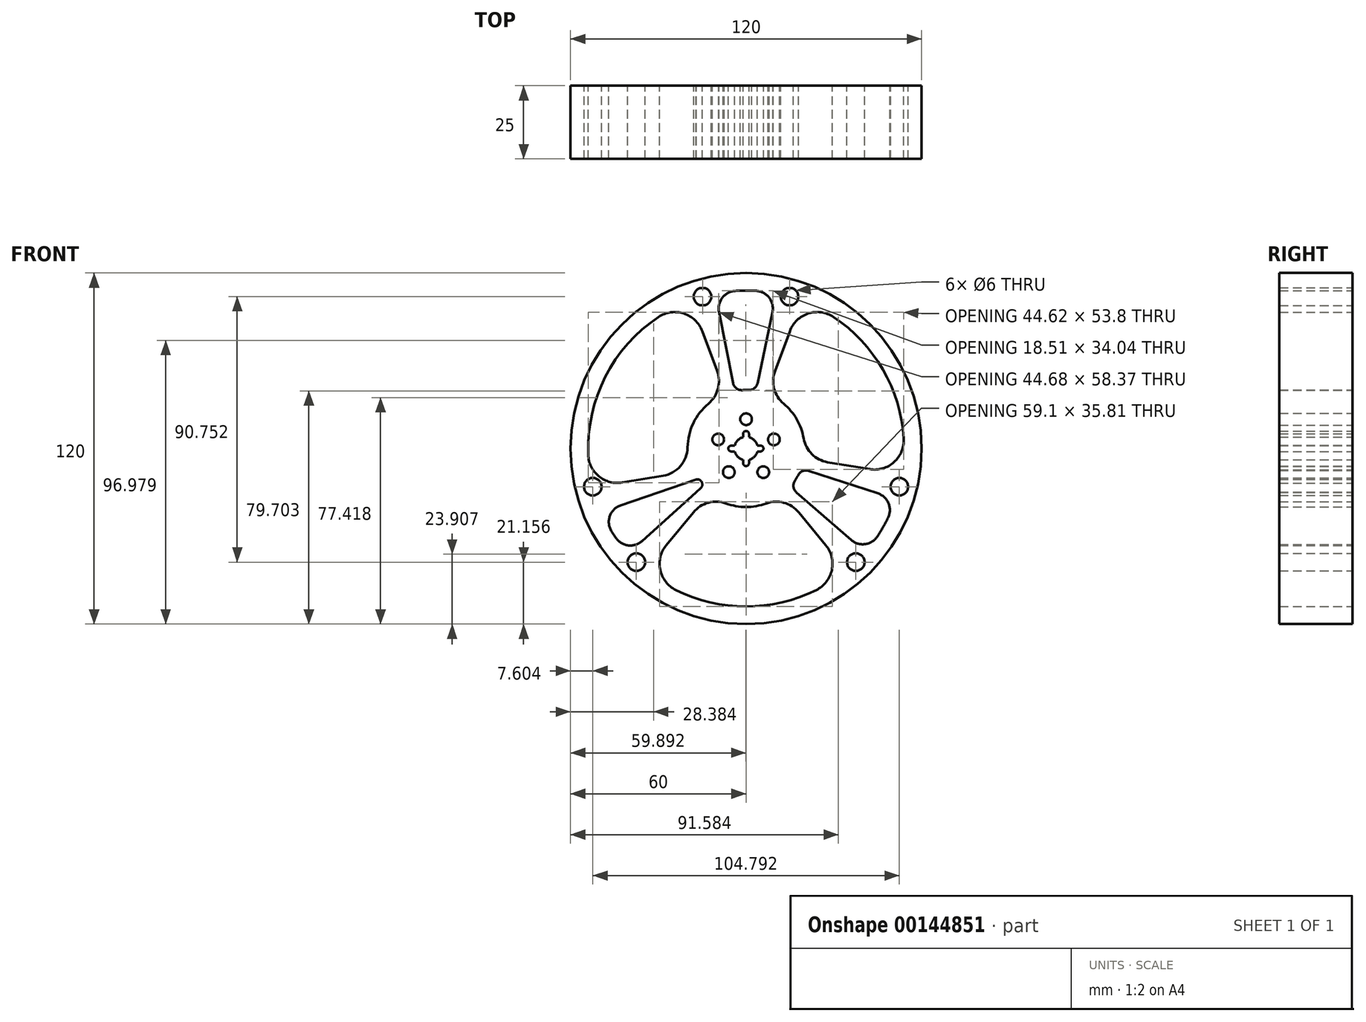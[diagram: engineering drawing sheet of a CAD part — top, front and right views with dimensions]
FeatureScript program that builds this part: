
annotation { "Feature Type Name" : "Feature", "Feature Type Description" : "" }
export const myFeature = defineFeature(function(context is Context, id is Id, definition is map)
    precondition{}
    {
        {
            var Q0;
            Q0=qCreatedBy(makeId("Front.planeOp"),FACE);
            var sketch = newSketch(context, id + "F0", { "sketchPlane" : qUnion([Q0])});
            skArc(sketch, "E0", {"start": v(-6, 0.32) * mm, "mid": v(-6, 0) * mm, "end": v(-6, -0.32) * mm, "construction": true});
            skArc(sketch, "E1", {"start": v(-1, 3.87) * mm, "mid": v(-2.83, 2.83) * mm, "end": v(-3.87, 1) * mm});
            skCircle(sketch, "E2", {"center": v(0, 0) * mm, "radius": 15 * mm});
            skArc(sketch, "E3", {"start": v(1, 5) * mm, "mid": v(0, 6) * mm, "end": v(-1, 5) * mm});
            skArc(sketch, "E4", {"start": v(4.95, -1) * mm, "mid": v(5.95, 0) * mm, "end": v(4.95, 1) * mm});
            skArc(sketch, "E5", {"start": v(-1, -5.01) * mm, "mid": v(0, -6.01) * mm, "end": v(1, -5.01) * mm});
            skArc(sketch, "E6", {"start": v(-5.05, 1) * mm, "mid": v(-6.05, 0) * mm, "end": v(-5.05, -1) * mm});
            skLineSegment(sketch, "E7", {"start": v(-1, 5) * mm, "end": v(-1, 3.87) * mm});
            skLineSegment(sketch, "E8", {"start": v(1, 5) * mm, "end": v(1, 3.87) * mm});
            skLineSegment(sketch, "E9", {"start": v(4.95, 1) * mm, "end": v(3.87, 1) * mm});
            skLineSegment(sketch, "E10", {"start": v(4.95, -1) * mm, "end": v(3.87, -1) * mm});
            skLineSegment(sketch, "E11", {"start": v(1, -5.01) * mm, "end": v(1, -3.87) * mm});
            skLineSegment(sketch, "E12", {"start": v(-1, -5.01) * mm, "end": v(-1, -3.87) * mm});
            skLineSegment(sketch, "E13", {"start": v(-5.05, 1) * mm, "end": v(-3.87, 1) * mm});
            skLineSegment(sketch, "E14", {"start": v(-5.05, -1) * mm, "end": v(-3.87, -1) * mm});
            skArc(sketch, "E15.trimOffspring", {"start": v(3.87, 1) * mm, "mid": v(2.83, 2.83) * mm, "end": v(1, 3.87) * mm});
            skArc(sketch, "E16.trimOffspring", {"start": v(1, -3.87) * mm, "mid": v(2.83, -2.83) * mm, "end": v(3.87, -1) * mm});
            skArc(sketch, "E17.trimOffspring", {"start": v(-3.87, -1) * mm, "mid": v(-2.83, -2.83) * mm, "end": v(-1, -3.87) * mm});
            skCircle(sketch, "E18", {"center": v(0, 10) * mm, "radius": 2 * mm});
            skPoint(sketch, "E18.centerSnap0", {"position": v(0, 6) * mm});
            skCircle(sketch, "E19.1.0", {"center": v(-9.51, 3.1) * mm, "radius": 2 * mm});
            skCircle(sketch, "E19.2.0", {"center": v(-5.88, -8.1) * mm, "radius": 2 * mm});
            skCircle(sketch, "E19.3.0", {"center": v(5.88, -8.1) * mm, "radius": 2 * mm});
            skCircle(sketch, "E19.4.0", {"center": v(9.51, 3.1) * mm, "radius": 2 * mm});
            skArc(sketch, "E20.trimOffspring", {"start": v(-0.17, -6) * mm, "mid": v(0, -6) * mm, "end": v(0.17, -6) * mm, "construction": true});
            skArc(sketch, "E21", {"start": v(-6.86, -18.79) * mm, "mid": v(0, -20) * mm, "end": v(6.86, -18.79) * mm});
            skArc(sketch, "E22", {"start": v(-46.03, -28.24) * mm, "mid": v(-45.3, -29.4) * mm, "end": v(-44.53, -30.55) * mm});
            skCircle(sketch, "E23", {"center": v(0, 0) * mm, "radius": 60 * mm});
            skLineSegment(sketch, "E24", {"start": v(-14.06, 49.02) * mm, "end": v(-14.88, 51.9) * mm, "construction": true});
            skCircle(sketch, "E25", {"center": v(14.88, 51.9) * mm, "radius": 3 * mm});
            skCircle(sketch, "E26", {"center": v(-14.88, 51.9) * mm, "radius": 3 * mm});
            skLineSegment(sketch, "E27", {"start": v(-9.9, 26.5) * mm, "end": v(-15, 40.14) * mm});
            skLineSegment(sketch, "E28", {"start": v(9.9, 26.5) * mm, "end": v(15, 40.14) * mm});
            skLineSegment(sketch, "E29", {"start": v(-9.25, 46.72) * mm, "end": v(-4.43, 22.37) * mm});
            skCircle(sketch, "E30.1.0", {"center": v(-37.51, -38.84) * mm, "radius": 3 * mm});
            skCircle(sketch, "E30.1.1", {"center": v(-52.4, -13.06) * mm, "radius": 3 * mm});
            skLineSegment(sketch, "E30.1.3", {"start": v(-35.57, -31.62) * mm, "end": v(-17.1, -15.02) * mm});
            skCircle(sketch, "E30.2.0", {"center": v(52.4, -13.06) * mm, "radius": 3 * mm});
            skCircle(sketch, "E30.2.1", {"center": v(37.51, -38.84) * mm, "radius": 3 * mm});
            skLineSegment(sketch, "E30.2.2", {"start": v(27.9, -4.68) * mm, "end": v(42.26, -7.08) * mm});
            skLineSegment(sketch, "E30.2.3", {"start": v(45, -15.32) * mm, "end": v(21.4, -7.64) * mm});
            skLineSegment(sketch, "E31.trimOffspring", {"start": v(-18, -21.82) * mm, "end": v(-27.27, -33.05) * mm});
            skLineSegment(sketch, "E32.trimOffspring", {"start": v(-17, -10.54) * mm, "end": v(-42.86, -19.43) * mm});
            skLineSegment(sketch, "E33.trimOffspring", {"start": v(-28.35, -9.3) * mm, "end": v(-42.32, -11.64) * mm});
            skLineSegment(sketch, "E34.trimOffspring", {"start": v(17.2, -14.97) * mm, "end": v(35.92, -31.27) * mm});
            skLineSegment(sketch, "E35.trimOffspring", {"start": v(18.01, -21.82) * mm, "end": v(27.27, -33.06) * mm});
            skPoint(sketch, "E36.orphan", {"position": v(-0.28, -0.58) * mm});
            skPoint(sketch, "E37.orphan", {"position": v(0, -0.02) * mm});
            skLineSegment(sketch, "E38.trimOffspring", {"start": v(3.94, 22.36) * mm, "end": v(9.02, 46.67) * mm});
            skArc(sketch, "E39.trimOffspring", {"start": v(3.54, 53.88) * mm, "mid": v(-0.12, 54) * mm, "end": v(-3.78, 53.87) * mm});
            skLineSegment(sketch, "E40.trimOffspring", {"start": v(14.06, 49.02) * mm, "end": v(14.88, 51.9) * mm, "construction": true});
            skArc(sketch, "E41.trimOffspring", {"start": v(-29.9, 44.97) * mm, "mid": v(-48.1, 24.54) * mm, "end": v(-53.96, -2.18) * mm});
            skArc(sketch, "E42.trimOffspring", {"start": v(-12.84, 15.33) * mm, "mid": v(-18.04, 8.63) * mm, "end": v(-20, 0.37) * mm});
            skArc(sketch, "E43.trimOffspring", {"start": v(0.87, 19.98) * mm, "mid": v(-0.21, 20) * mm, "end": v(-1.3, 19.96) * mm});
            skArc(sketch, "E44.trimOffspring", {"start": v(19.7, 3.46) * mm, "mid": v(17.32, 10) * mm, "end": v(12.84, 15.33) * mm});
            skArc(sketch, "E45.trimOffspring", {"start": v(16.67, -11.05) * mm, "mid": v(17.26, -10.1) * mm, "end": v(17.8, -9.12) * mm});
            skArc(sketch, "E46.trimOffspring", {"start": v(53.9, 3.42) * mm, "mid": v(46.76, 27) * mm, "end": v(29.9, 44.97) * mm});
            skArc(sketch, "E47.trimOffspring", {"start": v(44.84, -30.09) * mm, "mid": v(46.8, -26.94) * mm, "end": v(48.54, -23.66) * mm});
            skArc(sketch, "E48.trimOffspring", {"start": v(-24, -48.37) * mm, "mid": v(0, -54) * mm, "end": v(24, -48.37) * mm});
            skPoint(sketch, "E49.visualSharp", {"position": v(-49.45, -21.7) * mm});
            skArc(sketch, "E49.filletArc", {"start": v(-42.86, -19.43) * mm, "mid": v(-46.56, -23.07) * mm, "end": v(-46.03, -28.24) * mm});
            skPoint(sketch, "E50.visualSharp", {"position": v(-40.33, -35.9) * mm});
            skArc(sketch, "E50.filletArc", {"start": v(-44.53, -30.55) * mm, "mid": v(-40.29, -33.12) * mm, "end": v(-35.57, -31.62) * mm});
            skPoint(sketch, "E51.visualSharp", {"position": v(40.73, -35.46) * mm});
            skArc(sketch, "E51.filletArc", {"start": v(35.92, -31.27) * mm, "mid": v(40.65, -32.7) * mm, "end": v(44.84, -30.09) * mm});
            skPoint(sketch, "E52.visualSharp", {"position": v(51.15, -17.32) * mm});
            skArc(sketch, "E52.filletArc", {"start": v(48.54, -23.66) * mm, "mid": v(48.67, -18.69) * mm, "end": v(45, -15.32) * mm});
            skPoint(sketch, "E53.visualSharp", {"position": v(10.34, 53) * mm});
            skArc(sketch, "E53.filletArc", {"start": v(9.02, 46.67) * mm, "mid": v(7.92, 51.53) * mm, "end": v(3.54, 53.88) * mm});
            skPoint(sketch, "E54.visualSharp", {"position": v(-10.49, 52.97) * mm});
            skArc(sketch, "E54.filletArc", {"start": v(-3.78, 53.87) * mm, "mid": v(-8.13, 51.53) * mm, "end": v(-9.25, 46.72) * mm});
            skPoint(sketch, "E55.visualSharp", {"position": v(-52.33, -13.31) * mm});
            skArc(sketch, "E55.filletArc", {"start": v(-53.96, -2.18) * mm, "mid": v(-50.27, -9.54) * mm, "end": v(-42.32, -11.64) * mm});
            skPoint(sketch, "E56.visualSharp", {"position": v(-18.9, 50.59) * mm});
            skArc(sketch, "E56.filletArc", {"start": v(-15, 40.14) * mm, "mid": v(-21.28, 46.16) * mm, "end": v(-29.9, 44.97) * mm});
            skPoint(sketch, "E57.visualSharp", {"position": v(18.9, 50.59) * mm});
            skArc(sketch, "E57.filletArc", {"start": v(29.9, 44.97) * mm, "mid": v(21.28, 46.16) * mm, "end": v(15, 40.14) * mm});
            skPoint(sketch, "E58.visualSharp", {"position": v(53.26, -8.91) * mm});
            skArc(sketch, "E58.filletArc", {"start": v(42.26, -7.08) * mm, "mid": v(50.61, -4.64) * mm, "end": v(53.9, 3.42) * mm});
            skPoint(sketch, "E59.visualSharp", {"position": v(34.36, -41.66) * mm});
            skArc(sketch, "E59.filletArc", {"start": v(24, -48.37) * mm, "mid": v(29.33, -41.5) * mm, "end": v(27.27, -33.06) * mm});
            skPoint(sketch, "E60.visualSharp", {"position": v(-34.36, -41.65) * mm});
            skArc(sketch, "E60.filletArc", {"start": v(-27.27, -33.05) * mm, "mid": v(-29.33, -41.5) * mm, "end": v(-24, -48.37) * mm});
            skPoint(sketch, "E61.visualSharp", {"position": v(7, 18.74) * mm});
            skArc(sketch, "E61.filletArc", {"start": v(9.9, 26.5) * mm, "mid": v(9.6, 20.45) * mm, "end": v(12.84, 15.33) * mm});
            skPoint(sketch, "E62.visualSharp", {"position": v(19.72, -3.31) * mm});
            skArc(sketch, "E62.filletArc", {"start": v(19.7, 3.46) * mm, "mid": v(22.5, -1.92) * mm, "end": v(27.9, -4.68) * mm});
            skPoint(sketch, "E63.visualSharp", {"position": v(-3.88, 19.62) * mm});
            skArc(sketch, "E63.filletArc", {"start": v(-4.43, 22.37) * mm, "mid": v(-3.31, 20.57) * mm, "end": v(-1.3, 19.96) * mm});
            skPoint(sketch, "E64.visualSharp", {"position": v(3.38, 19.71) * mm});
            skArc(sketch, "E64.filletArc", {"start": v(0.87, 19.98) * mm, "mid": v(2.84, 20.6) * mm, "end": v(3.94, 22.36) * mm});
            skPoint(sketch, "E65.visualSharp", {"position": v(18.81, -6.8) * mm});
            skArc(sketch, "E65.filletArc", {"start": v(21.4, -7.64) * mm, "mid": v(19.33, -7.71) * mm, "end": v(17.8, -9.12) * mm});
            skPoint(sketch, "E66.visualSharp", {"position": v(15.08, -13.13) * mm});
            skArc(sketch, "E66.filletArc", {"start": v(16.67, -11.05) * mm, "mid": v(16.2, -13.11) * mm, "end": v(17.2, -14.97) * mm});
            skLineSegment(sketch, "E67", {"start": v(-17.1, -15.02) * mm, "end": v(-16.97, -14.89) * mm});
            skPoint(sketch, "E68.visualSharp", {"position": v(-7, 18.74) * mm});
            skArc(sketch, "E68.filletArc", {"start": v(-12.84, 15.33) * mm, "mid": v(-9.6, 20.45) * mm, "end": v(-9.9, 26.5) * mm});
            skPoint(sketch, "E69.visualSharp", {"position": v(-18.47, -7.66) * mm});
            skArc(sketch, "E69.filletArc", {"start": v(-28.35, -9.3) * mm, "mid": v(-22.42, -5.98) * mm, "end": v(-20, 0.37) * mm});
            skPoint(sketch, "E70.visualSharp", {"position": v(12.74, -15.42) * mm});
            skArc(sketch, "E70.filletArc", {"start": v(18.01, -21.82) * mm, "mid": v(12.92, -18.53) * mm, "end": v(6.86, -18.79) * mm});
            skPoint(sketch, "E71.visualSharp", {"position": v(-12.73, -15.43) * mm});
            skArc(sketch, "E71.filletArc", {"start": v(-6.86, -18.79) * mm, "mid": v(-12.9, -18.53) * mm, "end": v(-18, -21.82) * mm});
            skLineSegment(sketch, "E72", {"start": v(-16.97, -14.89) * mm, "end": v(-15.53, -13.59) * mm});
            skArc(sketch, "E73", {"start": v(-15.53, -13.59) * mm, "mid": v(-15.12, -11.52) * mm, "end": v(-17, -10.54) * mm});
            skSolve(sketch);
        }
        {
            var Q0;
            Q0 = qSketchRegion(id + "F0", true);
            var Q1;
            Q1=makeQuery(id+"F0.imprint","IMPRINT",FACE,{"disambiguationData":[TD([[makeQuery(id+"F0.imprint","IMPRINT",EDGE,{"derivedFrom":sQuery(id+"F0.wireOp",EDGE,"E1")}),-1.0]])]});
            var Q2;
            Q2 = qSketchRegion(id + "F2", true);
            extrude(context, id + "F1", {"entities" : qUnion([Q0, Q1, Q2]), "depth" : 25 * mm});
        }
    });
